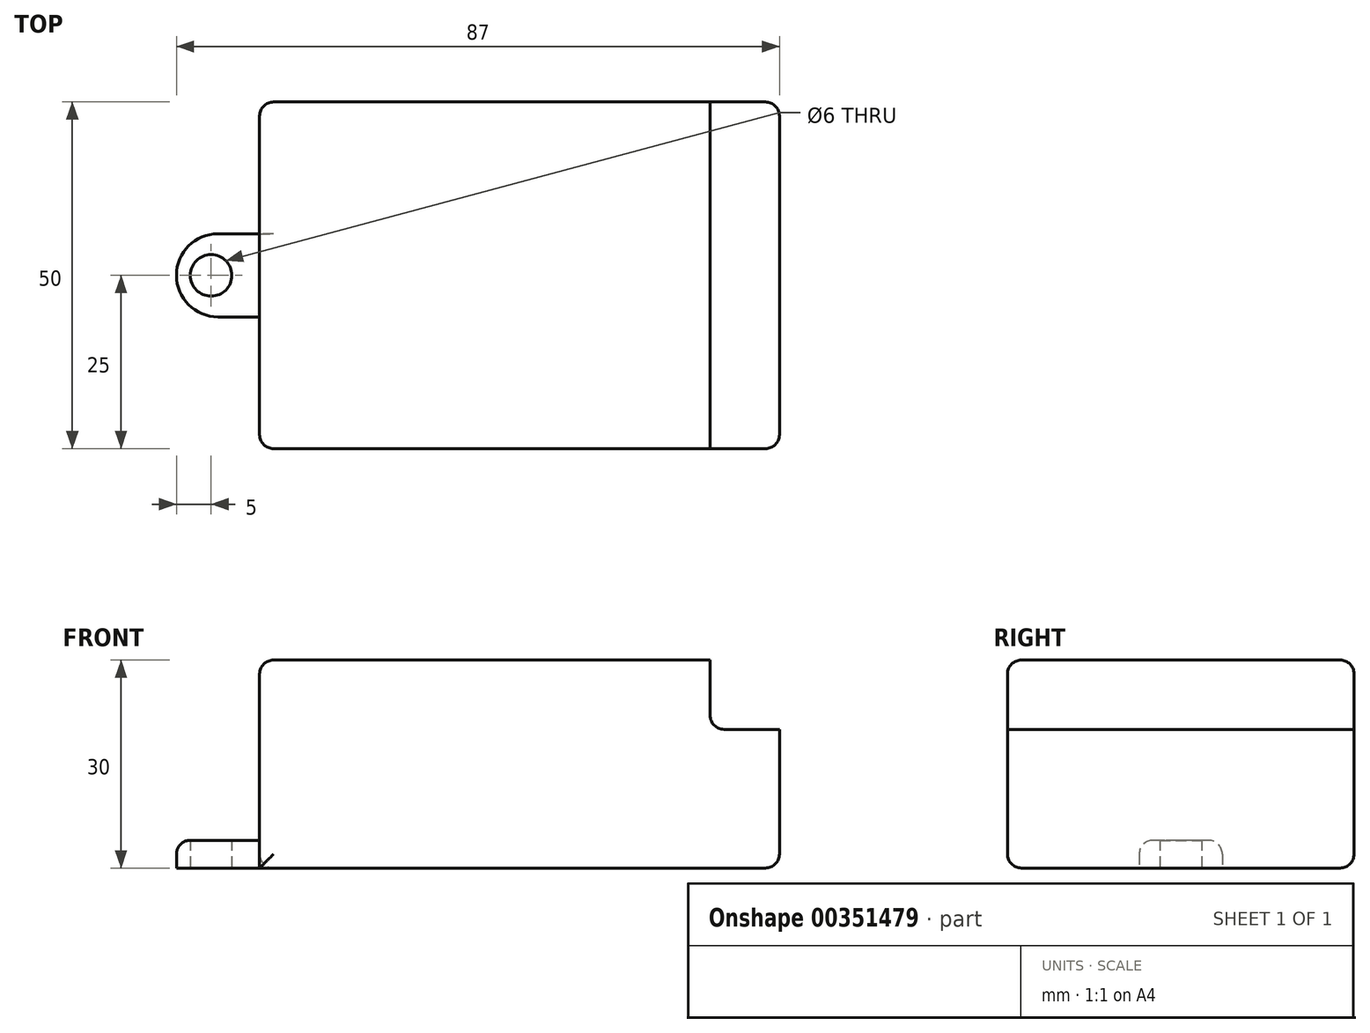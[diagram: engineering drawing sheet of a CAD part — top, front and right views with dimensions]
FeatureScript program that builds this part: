
annotation { "Feature Type Name" : "Feature", "Feature Type Description" : "" }
export const myFeature = defineFeature(function(context is Context, id is Id, definition is map)
    precondition{}
    {
        {
            var Q0;
            Q0=qCreatedBy(makeId("Top.planeOp"),FACE);
            var sketch = newSketch(context, id + "F0", { "sketchPlane" : qUnion([Q0])});
            skLineSegment(sketch, "E0.bottom", {"start": v(0, 25) * mm, "end": v(75, 25) * mm});
            skLineSegment(sketch, "E0.top", {"start": v(0, -25) * mm, "end": v(75, -25) * mm});
            skLineSegment(sketch, "E0.left", {"start": v(0, 25) * mm, "end": v(0, -25) * mm});
            skLineSegment(sketch, "E0.right", {"start": v(75, 25) * mm, "end": v(75, -25) * mm});
            skSolve(sketch);
        }
        {
            var Q0;
            Q0 = qSketchRegion(id + "F0", true);
            extrude(context, id + "F1", {"entities" : qUnion([Q0]), "depth" : 30 * mm});
        }
        {
            var Q0;
            Q0=makeQuery(id+"F1.opExtrude","CAP_FACE",FACE,{"disambiguationData":[OSD([sQuery(id+"F0.wireOp",EDGE,"E0.bottom"),sQuery(id+"F0.wireOp",EDGE,"E0.top"),sQuery(id+"F0.wireOp",EDGE,"E0.left"),sQuery(id+"F0.wireOp",EDGE,"E0.right")])],"isStart":false});
            var sketch = newSketch(context, id + "F2", { "sketchPlane" : qUnion([Q0])});
            skLineSegment(sketch, "E1.0", {"start": v(75, 25) * mm, "end": v(75, -25) * mm});
            skLineSegment(sketch, "E2", {"start": v(75, 25) * mm, "end": v(65, 25) * mm});
            skLineSegment(sketch, "E3", {"start": v(65, 25) * mm, "end": v(65, -25) * mm});
            skLineSegment(sketch, "E4", {"start": v(65, -25) * mm, "end": v(75, -25) * mm});
            skLineSegment(sketch, "E5", {"start": v(75, -25) * mm, "end": v(65, -25) * mm});
            skSolve(sketch);
        }
        {
            var Q0;
            Q0=makeQuery(id+"F2.imprint","IMPRINT",FACE,{"disambiguationData":[TD([[makeQuery(id+"F2.imprint","IMPRINT",EDGE,{"derivedFrom":sQuery(id+"F2.wireOp",EDGE,"E1.0")}),-1.0]])]});
            extrude(context, id + "F3", {"entities" : qUnion([Q0]), "operationType" : NewBodyOperationType.REMOVE, "oppositeDirection" : true, "depth" : 10 * mm});
        }
        {
            var Q0;
            Q0=qCreatedBy(makeId("Top.planeOp"),FACE);
            var sketch = newSketch(context, id + "F4", { "sketchPlane" : qUnion([Q0])});
            skLineSegment(sketch, "E6.0", {"start": v(0, 25) * mm, "end": v(0, -25) * mm});
            skLineSegment(sketch, "E7.bottom", {"start": v(0, 6) * mm, "end": v(-12, 6) * mm});
            skLineSegment(sketch, "E7.top", {"start": v(0, -6) * mm, "end": v(-12, -6) * mm});
            skLineSegment(sketch, "E7.left", {"start": v(0, 6) * mm, "end": v(0, -6) * mm});
            skLineSegment(sketch, "E7.right", {"start": v(-12, 6) * mm, "end": v(-12, -6) * mm});
            skCircle(sketch, "E8", {"center": v(-7, 0) * mm, "radius": 3 * mm});
            skSolve(sketch);
        }
        {
            var Q0;
            Q0=makeQuery(id+"F4.imprint","IMPRINT",FACE,{"disambiguationData":[TD([[makeQuery(id+"F4.imprint","IMPRINT",EDGE,{"derivedFrom":sQuery(id+"F4.wireOp",EDGE,"E7.bottom")}),1.0]])]});
            extrude(context, id + "F5", {"entities" : qUnion([Q0]), "operationType" : NewBodyOperationType.ADD, "depth" : 4 * mm});
        }
        {
            var Q0;
            Q0=makeQuery(id+"F5.opExtrude","SWEPT_EDGE",EDGE,{"disambiguationData":[OSD([sQuery(id+"F4.wireOp",EDGE,"E7.top"),sQuery(id+"F4.wireOp",EDGE,"E7.left")])]});
            var Q1;
            Q1=makeQuery(id+"F5.opExtrude","SWEPT_EDGE",EDGE,{"disambiguationData":[OSD([sQuery(id+"F4.wireOp",EDGE,"E7.bottom"),sQuery(id+"F4.wireOp",EDGE,"E7.left")])]});
            var Q2;
            Q2=makeQuery(id+"F5.opExtrude","SWEPT_EDGE",EDGE,{"disambiguationData":[OSD([sQuery(id+"F4.wireOp",EDGE,"E7.bottom"),sQuery(id+"F4.wireOp",EDGE,"E7.right")])]});
            var Q3;
            Q3=makeQuery(id+"F5.opExtrude","SWEPT_EDGE",EDGE,{"disambiguationData":[OSD([sQuery(id+"F4.wireOp",EDGE,"E7.top"),sQuery(id+"F4.wireOp",EDGE,"E7.right")])]});
            fillet(context, id + "F6", {"entities" : qUnion([Q0, Q1, Q2, Q3]), "radius" : 6 * mm, "tangentPropagation" : true, "allowEdgeOverflow" : false});
        }
        {
            var Q0;
            Q0=makeQuery(id+"F1.opExtrude","CAP_EDGE",EDGE,{"disambiguationData":[OSD([sQuery(id+"F0.wireOp",EDGE,"E0.top")])],"isStart":false});
            var Q1;
            Q1=makeQuery(id+"F1.opExtrude","CAP_EDGE",EDGE,{"disambiguationData":[OSD([sQuery(id+"F0.wireOp",EDGE,"E0.left")])],"isStart":false});
            var Q2;
            Q2=makeQuery(id+"F1.opExtrude","SWEPT_EDGE",EDGE,{"disambiguationData":[OSD([sQuery(id+"F0.wireOp",EDGE,"E0.top"),sQuery(id+"F0.wireOp",EDGE,"E0.left")])]});
            var Q3;
            Q3=makeQuery(id+"F1.opExtrude","CAP_EDGE",EDGE,{"disambiguationData":[OSD([sQuery(id+"F0.wireOp",EDGE,"E0.bottom")])],"isStart":false});
            var Q4;
            Q4=makeQuery(id+"F1.opExtrude","SWEPT_EDGE",EDGE,{"disambiguationData":[OSD([sQuery(id+"F0.wireOp",EDGE,"E0.bottom"),sQuery(id+"F0.wireOp",EDGE,"E0.left")])]});
            var Q5;
            Q5=makeQuery(id+"F3.boolean.opBoolean","COPY",EDGE,{"derivedFrom":makeQuery(id+"F3.opExtrude","CAP_EDGE",EDGE,{"disambiguationData":[OSD([sQuery(id+"F2.wireOp",EDGE,"E3")])],"isStart":true})});
            var Q6;
            Q6=makeQuery(id+"F3.boolean.opBoolean","COPY",EDGE,{"derivedFrom":makeQuery(id+"F3.opExtrude","SWEPT_EDGE",EDGE,{"disambiguationData":[OSD([sQuery(id+"F0.wireOp",EDGE,"E0.top"),sQuery(id+"F2.wireOp",EDGE,"E3"),sQuery(id+"F2.wireOp",EDGE,"E5")])]})});
            var Q7;
            Q7=makeQuery(id+"F3.boolean.opBoolean","COPY",EDGE,{"derivedFrom":makeQuery(id+"F3.opExtrude","SWEPT_EDGE",EDGE,{"disambiguationData":[OSD([sQuery(id+"F0.wireOp",EDGE,"E0.bottom"),sQuery(id+"F2.wireOp",EDGE,"E2"),sQuery(id+"F2.wireOp",EDGE,"E3")])]})});
            var Q8;
            Q8=makeQuery(id+"F3.boolean.opBoolean","COPY",EDGE,{"derivedFrom":makeQuery(id+"F3.opExtrude","CAP_EDGE",EDGE,{"disambiguationData":[OSD([sQuery(id+"F2.wireOp",EDGE,"E3")])],"isStart":false})});
            var Q9;
            Q9=makeQuery(id+"F3.boolean.opBoolean","COPY",EDGE,{"derivedFrom":makeQuery(id+"F3.opExtrude","CAP_EDGE",EDGE,{"disambiguationData":[OSD([sQuery(id+"F2.wireOp",EDGE,"E1.0")])],"isStart":false})});
            var Q10;
            Q10=makeQuery(id+"F1.opExtrude","SWEPT_EDGE",EDGE,{"disambiguationData":[OSD([sQuery(id+"F0.wireOp",EDGE,"E0.top"),sQuery(id+"F0.wireOp",EDGE,"E0.right")])]});
            var Q11;
            Q11=makeQuery(id+"F1.opExtrude","SWEPT_EDGE",EDGE,{"disambiguationData":[OSD([sQuery(id+"F0.wireOp",EDGE,"E0.bottom"),sQuery(id+"F0.wireOp",EDGE,"E0.right")])]});
            var Q12;
            Q12=makeQuery(id+"F1.opExtrude","CAP_EDGE",EDGE,{"disambiguationData":[OSD([sQuery(id+"F0.wireOp",EDGE,"E0.right")])],"isStart":true});
            var Q13;
            Q13=makeQuery(id+"F1.opExtrude","CAP_EDGE",EDGE,{"disambiguationData":[OSD([sQuery(id+"F0.wireOp",EDGE,"E0.top")])],"isStart":true});
            var Q14;
            Q14=makeQuery(id+"F1.opExtrude","CAP_EDGE",EDGE,{"disambiguationData":[OSD([sQuery(id+"F0.wireOp",EDGE,"E0.bottom")])],"isStart":true});
            var Q15;
            {var subQ1=sQuery(id+"F0.wireOp",EDGE,"E0.left");var subQ2=sQuery(id+"F0.wireOp",EDGE,"E0.bottom");Q15=makeQuery(id+"F5.boolean.opBoolean","SPLIT",EDGE,{"disambiguationData":[TD([makeQuery(id+"F1.opExtrude","SWEPT_FACE",FACE,{"disambiguationData":[OSD([subQ2])]})])],"derivedFrom":makeQuery(id+"F1.opExtrude","CAP_EDGE",EDGE,{"disambiguationData":[OSD([subQ1])],"isStart":true})});}
            var Q16;
            {var subQ0=sQuery(id+"F4.wireOp",EDGE,"E7.left");var subQ1=sQuery(id+"F4.wireOp",EDGE,"E7.bottom");Q16=makeQuery(id+"F6.opFillet","BLEND_EDGE",EDGE,{"blendedFrom":[makeQuery(id+"F5.opExtrude","SWEPT_EDGE",EDGE,{"disambiguationData":[OSD([subQ1,subQ0])]}),makeQuery(id+"F5.opExtrude","CAP_FACE",FACE,{"disambiguationData":[OSD([subQ1,sQuery(id+"F4.wireOp",EDGE,"E7.top"),subQ0,sQuery(id+"F4.wireOp",EDGE,"E7.right"),sQuery(id+"F4.wireOp",EDGE,"E8")])],"isStart":false})],"blendedInto":[makeQuery(id+"F5.opExtrude","CAP_FACE",FACE,{"disambiguationData":[OSD([subQ1,sQuery(id+"F4.wireOp",EDGE,"E7.top"),subQ0,sQuery(id+"F4.wireOp",EDGE,"E7.right"),sQuery(id+"F4.wireOp",EDGE,"E8")])],"isStart":false})]});}
            fillet(context, id + "F7", {"entities" : qUnion([Q0, Q1, Q2, Q3, Q4, Q5, Q6, Q7, Q8, Q9, Q10, Q11, Q12, Q13, Q14, Q15, Q16]), "radius" : 2 * mm, "tangentPropagation" : true, "allowEdgeOverflow" : false});
        }
    });
